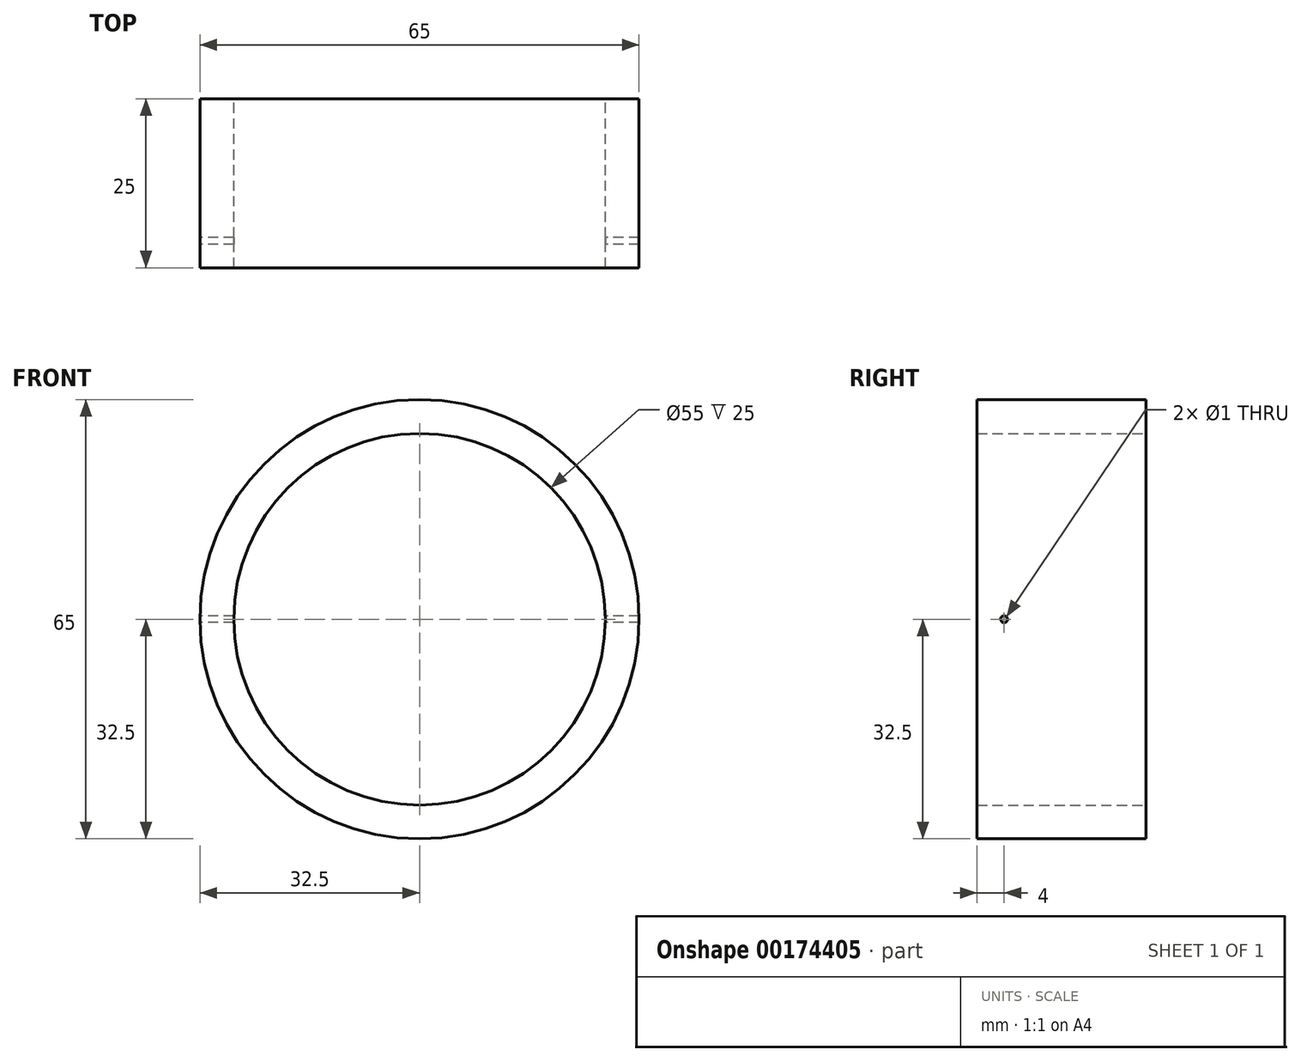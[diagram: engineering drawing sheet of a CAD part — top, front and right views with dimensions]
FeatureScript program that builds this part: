
annotation { "Feature Type Name" : "Feature", "Feature Type Description" : "" }
export const myFeature = defineFeature(function(context is Context, id is Id, definition is map)
    precondition{}
    {
        {
            var Q0;
            Q0=qCreatedBy(makeId("Front.planeOp"),FACE);
            var sketch = newSketch(context, id + "F0", { "sketchPlane" : qUnion([Q0])});
            skCircle(sketch, "E0", {"center": v(0, 0) * mm, "radius": 27.5 * mm});
            skCircle(sketch, "E1.0", {"center": v(0, 0) * mm, "radius": 32.5 * mm});
            skSolve(sketch);
        }
        {
            var Q0;
            Q0=qSketchRegion(id+"F0",true);
            extrude(context, id + "F1", {"entities" : qUnion([Q0]), "depth" : 25 * mm});
        }
        {
            var Q0;
            Q0=qCreatedBy(makeId("Top.planeOp"),FACE);
            var sketch = newSketch(context, id + "F2", { "sketchPlane" : qUnion([Q0])});
            skCircle(sketch, "E2", {"center": v(0, -22) * mm, "radius": 0.5 * mm});
            skSolve(sketch);
        }
        {
            var Q0;
            Q0=qCreatedBy(makeId("Right.planeOp"),FACE);
            var sketch = newSketch(context, id + "F3", { "sketchPlane" : qUnion([Q0])});
            skCircle(sketch, "E3", {"center": v(-21, 0) * mm, "radius": 0.5 * mm});
            skSolve(sketch);
        }
        {
            var Q0;
            Q0=qSketchRegion(id+"F3",true);
            extrude(context, id + "F4", {"entities" : qUnion([Q0]), "operationType" : NewBodyOperationType.REMOVE, "endBound" : BoundingType.THROUGH_ALL, "depth" : 25 * mm, "hasSecondDirection" : true, "secondDirectionBound" : SecondDirectionBoundingType.THROUGH_ALL, "secondDirectionOppositeDirection" : true, "secondDirectionDepth" : 25 * mm});
        }
    });
